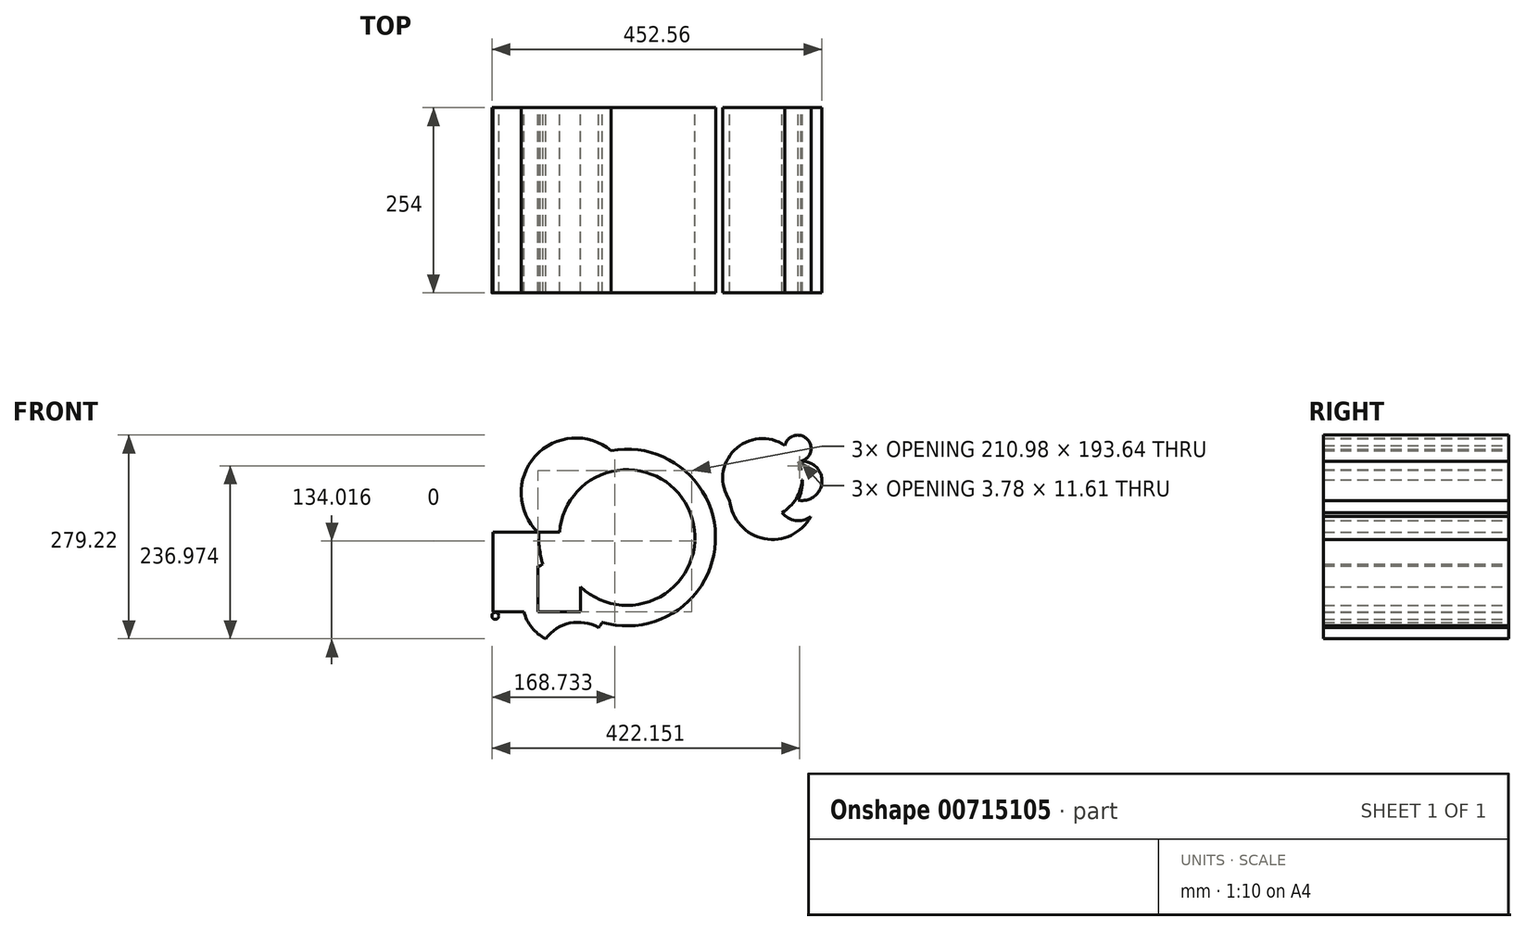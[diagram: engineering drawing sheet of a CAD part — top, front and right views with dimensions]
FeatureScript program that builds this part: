
annotation { "Feature Type Name" : "Feature", "Feature Type Description" : "" }
export const myFeature = defineFeature(function(context is Context, id is Id, definition is map)
    precondition{}
    {
        {
            var Q0;
            Q0=qCreatedBy(makeId("Front.planeOp"),FACE);
            var sketch = newSketch(context, id + "F0", { "sketchPlane" : qUnion([Q0])});
            skLineSegment(sketch, "E0.bottom", {"start": v(-237.39, -55.2) * mm, "end": v(-175.76, -55.2) * mm});
            skLineSegment(sketch, "E0.top", {"start": v(-237.39, -117.85) * mm, "end": v(-175.76, -117.85) * mm});
            skLineSegment(sketch, "E0.left", {"start": v(-237.39, -55.2) * mm, "end": v(-237.39, -117.85) * mm});
            skLineSegment(sketch, "E0.right", {"start": v(-175.76, -55.2) * mm, "end": v(-175.76, -117.85) * mm});
            skLineSegment(sketch, "E1.top", {"start": v(-237.39, -9.14) * mm, "end": v(-175.76, -9.14) * mm});
            skLineSegment(sketch, "E1.left", {"start": v(-237.39, -55.2) * mm, "end": v(-237.39, -9.14) * mm});
            skLineSegment(sketch, "E1.right", {"start": v(-175.76, -55.2) * mm, "end": v(-175.76, -9.14) * mm});
            skLineSegment(sketch, "E2.bottom", {"start": v(-175.76, -9.14) * mm, "end": v(-117.26, -9.14) * mm});
            skLineSegment(sketch, "E2.top", {"start": v(-175.76, -55.2) * mm, "end": v(-117.26, -55.2) * mm});
            skLineSegment(sketch, "E2.left", {"start": v(-175.76, -9.14) * mm, "end": v(-175.76, -55.2) * mm});
            skLineSegment(sketch, "E2.right", {"start": v(-117.26, -9.14) * mm, "end": v(-117.26, -55.2) * mm});
            skLineSegment(sketch, "E3.bottom", {"start": v(-117.26, -55.2) * mm, "end": v(-175.76, -55.2) * mm});
            skLineSegment(sketch, "E3.top", {"start": v(-117.26, -117.85) * mm, "end": v(-175.76, -117.85) * mm});
            skLineSegment(sketch, "E3.left", {"start": v(-117.26, -55.2) * mm, "end": v(-117.26, -117.85) * mm});
            skCircle(sketch, "E4", {"center": v(-234.25, -123.77) * mm, "radius": 4.75 * mm});
            skArc(sketch, "E5", {"start": v(-92.7, -139.84) * mm, "mid": v(-131.9, -133.63) * mm, "end": v(-165.3, -155.05) * mm});
            skArc(sketch, "E6", {"start": v(-92.7, -139.84) * mm, "mid": v(-150.42, -45.25) * mm, "end": v(-165.3, -155.05) * mm});
            skCircle(sketch, "E7", {"center": v(-123.53, 45.04) * mm, "radius": 75.26 * mm});
            skCircle(sketch, "E8", {"center": v(-53.54, -16.24) * mm, "radius": 64.12 * mm});
            skCircle(sketch, "E9", {"center": v(-53.54, -16.24) * mm, "radius": 74.7 * mm});
            skCircle(sketch, "E10", {"center": v(-53.54, -16.24) * mm, "radius": 121.2 * mm});
            skCircle(sketch, "E11", {"center": v(-53.54, -16.24) * mm, "radius": 93.02 * mm});
            skLineSegment(sketch, "E12.bottom", {"start": v(-53.54, -16.24) * mm, "end": v(-16.45, -16.24) * mm});
            skLineSegment(sketch, "E12.top", {"start": v(-53.54, 5.96) * mm, "end": v(-16.45, 5.96) * mm});
            skLineSegment(sketch, "E12.left", {"start": v(-53.54, -16.24) * mm, "end": v(-53.54, 5.96) * mm});
            skLineSegment(sketch, "E12.right", {"start": v(-16.45, -16.24) * mm, "end": v(-16.45, 5.96) * mm});
            skLineSegment(sketch, "E13.bottom", {"start": v(-16.45, 5.96) * mm, "end": v(-58.76, 5.96) * mm});
            skLineSegment(sketch, "E13.top", {"start": v(-16.45, 25.08) * mm, "end": v(-58.76, 25.08) * mm});
            skLineSegment(sketch, "E13.left", {"start": v(-16.45, 5.96) * mm, "end": v(-16.45, 25.08) * mm});
            skLineSegment(sketch, "E13.right", {"start": v(-58.76, 5.96) * mm, "end": v(-58.76, 25.08) * mm});
            skLineSegment(sketch, "E14.bottom", {"start": v(-58.76, 25.08) * mm, "end": v(-16.45, 25.08) * mm});
            skLineSegment(sketch, "E14.top", {"start": v(-58.76, 36.06) * mm, "end": v(-16.45, 36.06) * mm});
            skLineSegment(sketch, "E14.left", {"start": v(-58.76, 25.08) * mm, "end": v(-58.76, 36.06) * mm});
            skLineSegment(sketch, "E14.right", {"start": v(-16.45, 25.08) * mm, "end": v(-16.45, 36.06) * mm});
            skArc(sketch, "E15", {"start": v(203.96, 51.83) * mm, "mid": v(153.36, 39.18) * mm, "end": v(198.22, 12.56) * mm});
            skArc(sketch, "E16", {"start": v(181.26, 35.1) * mm, "mid": v(213.56, 61.41) * mm, "end": v(181.26, 87.73) * mm});
            skArc(sketch, "E17", {"start": v(181.26, 35.1) * mm, "mid": v(186.69, 61.41) * mm, "end": v(181.26, 87.73) * mm});
            skArc(sketch, "E18", {"start": v(186.69, 28.34) * mm, "mid": v(219.38, 61.27) * mm, "end": v(181.26, 87.73) * mm});
            skArc(sketch, "E19", {"start": v(203.96, 51.83) * mm, "mid": v(87.38, 48.83) * mm, "end": v(198.22, 12.56) * mm});
            skArc(sketch, "E20", {"start": v(181.26, 87.73) * mm, "mid": v(194.47, 117.64) * mm, "end": v(162.7, 109.9) * mm});
            skArc(sketch, "E21", {"start": v(162.7, 109.9) * mm, "mid": v(90.22, 30.38) * mm, "end": v(181.26, 87.73) * mm});
            skArc(sketch, "E22", {"start": v(128.23, -39.5) * mm, "mid": v(248.3, 11.47) * mm, "end": v(162.7, 109.9) * mm});
            skSolve(sketch);
        }
        {
            var Q0;
            Q0 = qSketchRegion(id + "F0", true);
            extrude(context, id + "F1", {"entities" : qUnion([Q0]), "depth" : 254 * mm, "offsetDistance" : 25.4 * mm});
        }
    });
